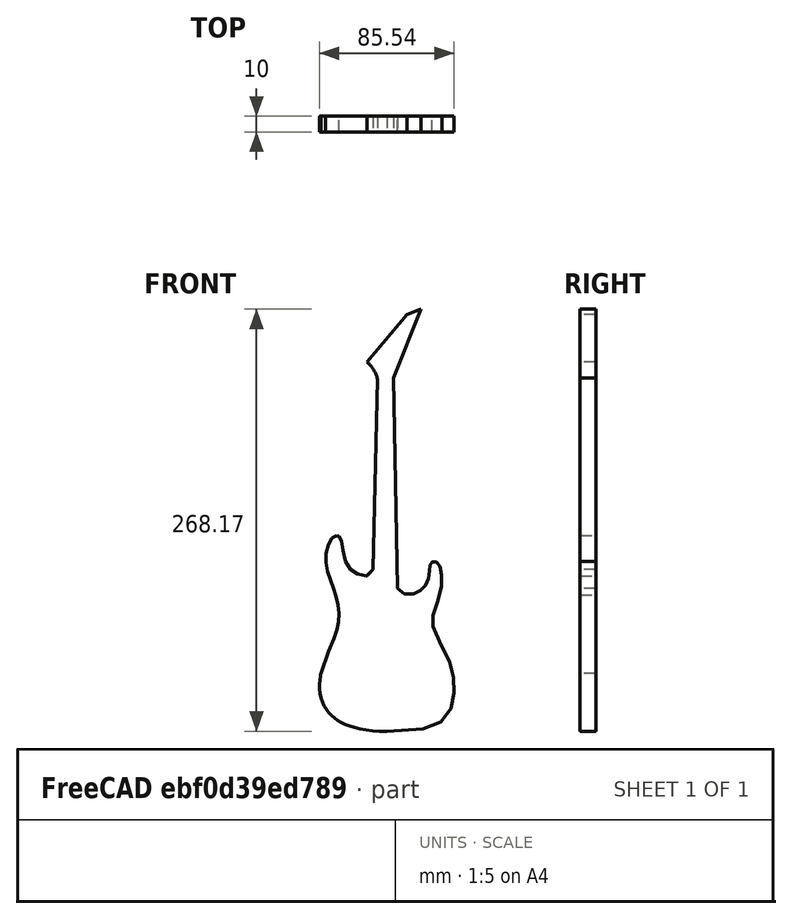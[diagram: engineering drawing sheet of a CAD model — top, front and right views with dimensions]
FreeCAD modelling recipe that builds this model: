
FCSTD DOCUMENT  (FreeCAD 0.19R23964 (Git))
Label: guitar
License: All rights reserved
LicenseURL: http://en.wikipedia.org/wiki/All_rights_reserved
objects: Image::ImagePlane×1, Sketcher::SketchObject×1, PartDesign::Pad×1, PartDesign::Body×1, App::Part×1
note: 4 computed .brp shape members not serialized (recipe doc carries the construction recipe); baked Part::Feature solids carry a one-line shape summary decoded from their .brp

FEATURE [Image::ImagePlane] ImagePlane
  Placement = pos=(0,0,0) rot=(-1,0,0;4.71239rad)
  XSize = 228
  YSize = 290
FEATURE [Sketcher::SketchObject] Sketch
  FullyConstrained = false
  MapMode = 5
  Placement = pos=(0,0,0) rot=(1,0,0;1.5708rad)
  Support = -> [XZ_Plane001]
  sketch-geometry (99):
    g0-g6: Circle x7 (B-spline internal-alignment scaffolding for g7; pole/knot coordinates omitted)
    g7: BSplineCurve PolesCount=7 KnotsCount=5 Degree=3 IsPeriodic=0
    g8-g12: GeomPoint x5 (B-spline internal-alignment scaffolding for g7; pole/knot coordinates omitted)
    g13-g27: Circle x15 (B-spline internal-alignment scaffolding for g28; pole/knot coordinates omitted)
    g28: BSplineCurve PolesCount=15 KnotsCount=13 Degree=3 IsPeriodic=0
    g29-g41: GeomPoint x13 (B-spline internal-alignment scaffolding for g28; pole/knot coordinates omitted)
    g42: LineSegment StartX=-8.87692 StartY=-31.057 StartZ=0 EndX=-6.0269 EndY=89.9126 EndZ=0
    g43-g46: Circle x4 (B-spline internal-alignment scaffolding for g47; pole/knot coordinates omitted)
    g47: BSplineCurve PolesCount=4 KnotsCount=2 Degree=3 IsPeriodic=0
    g48: GeomPoint X=-6.0269 Y=89.9126 Z=0
    g49: GeomPoint X=-12.5855 Y=100.473 Z=0
    g50: LineSegment StartX=-12.5855 StartY=100.473 StartZ=0 EndX=12.8395 EndY=130.872 EndZ=0
    g51: LineSegment StartX=12.8395 StartY=130.872 StartZ=0 EndX=21.7946 EndY=134.189 EndZ=0
    g52: LineSegment StartX=21.7946 StartY=134.189 StartZ=0 EndX=4.38191 EndY=90.4083 EndZ=0
    g53: LineSegment StartX=4.38191 StartY=90.4083 StartZ=0 EndX=6.86221 EndY=-43.1733 EndZ=0
    g54-g76: Circle x23 (B-spline internal-alignment scaffolding for g77; pole/knot coordinates omitted)
    g77: BSplineCurve PolesCount=23 KnotsCount=21 Degree=3 IsPeriodic=0
    g78-g98: GeomPoint x21 (B-spline internal-alignment scaffolding for g77; pole/knot coordinates omitted)
  constraints (30):
    c: PointOnObject(g7,g-2)
    c: Weight(g0) = 1
    c: Equal(g0, g1-g6) x6
    c: Coincident(g7,g5)
    c: InternalAlignment(g0-g6 -> g7) x7
    c: InternalAlignment(g8-g12 -> g7) x5
    c: Coincident(g28,g7)
    c: Weight(g13) = 1
    c: Equal(g13, g14-g27) x14
    c: InternalAlignment(g13-g27 -> g28) x15
    c: InternalAlignment(g29-g41 -> g28) x13
    c: Coincident(g42,g28)
    c: Coincident(g47,g42)
    c: Weight(g43) = 1
    c: Equal(g43,g44)
    c: Equal(g43,g45)
    c: Equal(g43,g46)
    c: InternalAlignment(g43-g46 -> g47) x4
    c: InternalAlignment(g48,g47)
    c: InternalAlignment(g49,g47)
    c: Coincident(g50,g47)
    c: Coincident(g50,g51)
    c: Coincident(g51,g52)
    c: Coincident(g52,g53)
    c: Coincident(g77,g53)
    c: Weight(g54) = 1
    c: Equal(g54, g55-g76) x22
    c: Coincident(g77,g7)
    c: InternalAlignment(g54-g76 -> g77) x23
    c: InternalAlignment(g78-g98 -> g77) x21
FEATURE [PartDesign::Pad] Pad
  Direction = (1,1,1)
  Length = 10
  Length2 = 100
  Placement = pos=(0,0,0) rot=(1,0,0;1.5708rad)
  Profile = -> Sketch
  Type = 0
FEATURE [PartDesign::Body] Body
  Group = -> [Sketch,Pad]
  Origin = -> Origin001
  Tip = -> Pad
FEATURE [App::Part] Part
  Group = -> [Body]
  Origin = -> Origin
